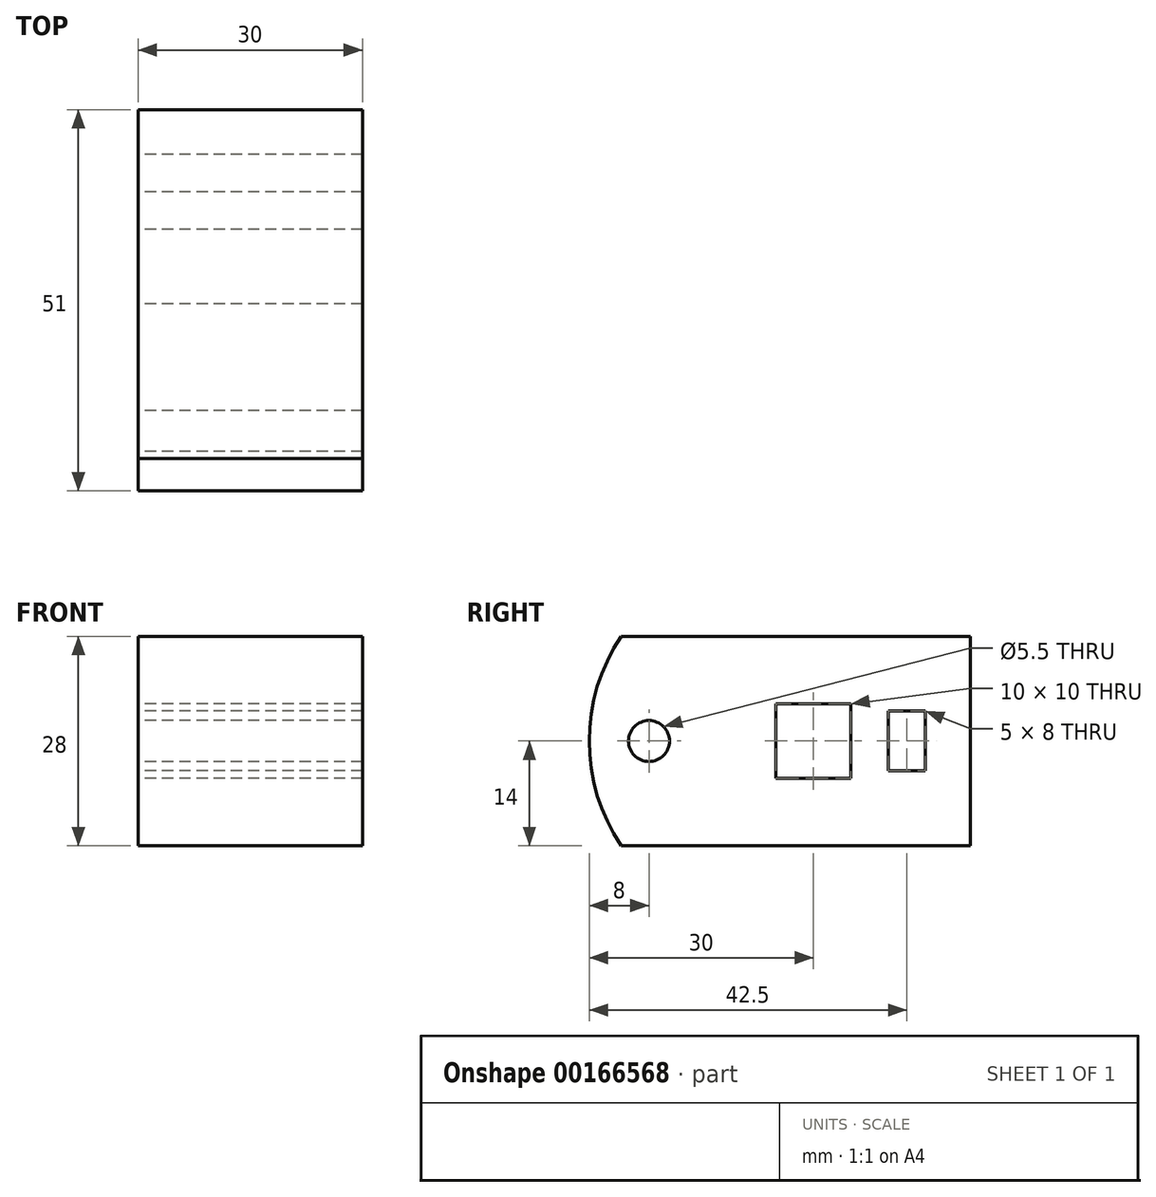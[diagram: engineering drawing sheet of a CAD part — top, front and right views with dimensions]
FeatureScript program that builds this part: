
annotation { "Feature Type Name" : "Feature", "Feature Type Description" : "" }
export const myFeature = defineFeature(function(context is Context, id is Id, definition is map)
    precondition{}
    {
        {
            var Q0;
            Q0=qCreatedBy(makeId("Right.planeOp"),FACE);
            var sketch = newSketch(context, id + "F0", { "sketchPlane" : qUnion([Q0])});
            skLineSegment(sketch, "E0.bottom", {"start": v(-3.71, 0) * mm, "end": v(43, 0) * mm});
            skLineSegment(sketch, "E0.top", {"start": v(-3.71, 28) * mm, "end": v(43, 28) * mm});
            skLineSegment(sketch, "E0.right", {"start": v(43, 0) * mm, "end": v(43, 28) * mm});
            skCircle(sketch, "E1", {"center": v(0, 14) * mm, "radius": 2.75 * mm});
            skLineSegment(sketch, "E2", {"start": v(0, 14) * mm, "end": v(43, 14) * mm, "construction": true});
            skLineSegment(sketch, "E3.bottom", {"start": v(32, 10) * mm, "end": v(37, 10) * mm});
            skLineSegment(sketch, "E3.top", {"start": v(32, 18) * mm, "end": v(37, 18) * mm});
            skLineSegment(sketch, "E3.left", {"start": v(32, 10) * mm, "end": v(32, 18) * mm});
            skLineSegment(sketch, "E3.right", {"start": v(37, 10) * mm, "end": v(37, 18) * mm});
            skPoint(sketch, "E3.middle", {"position": v(34.5, 14) * mm});
            skArc(sketch, "E4", {"start": v(-3.71, 28) * mm, "mid": v(-8, 14) * mm, "end": v(-3.71, 0) * mm});
            skPoint(sketch, "E5.orphan", {"position": v(-8, 0) * mm});
            skLineSegment(sketch, "E6.bottom", {"start": v(17, 19) * mm, "end": v(27, 19) * mm});
            skLineSegment(sketch, "E6.top", {"start": v(17, 9) * mm, "end": v(27, 9) * mm});
            skLineSegment(sketch, "E6.left", {"start": v(17, 19) * mm, "end": v(17, 9) * mm});
            skLineSegment(sketch, "E6.right", {"start": v(27, 19) * mm, "end": v(27, 9) * mm});
            skPoint(sketch, "E6.middle", {"position": v(22, 14) * mm});
            skSolve(sketch);
        }
        {
            var Q0;
            Q0 = qSketchRegion(id + "F0", true);
            extrude(context, id + "F1", {"entities" : qUnion([Q0]), "endBound" : BoundingType.SYMMETRIC, "depth" : 30 * mm});
        }
    });
